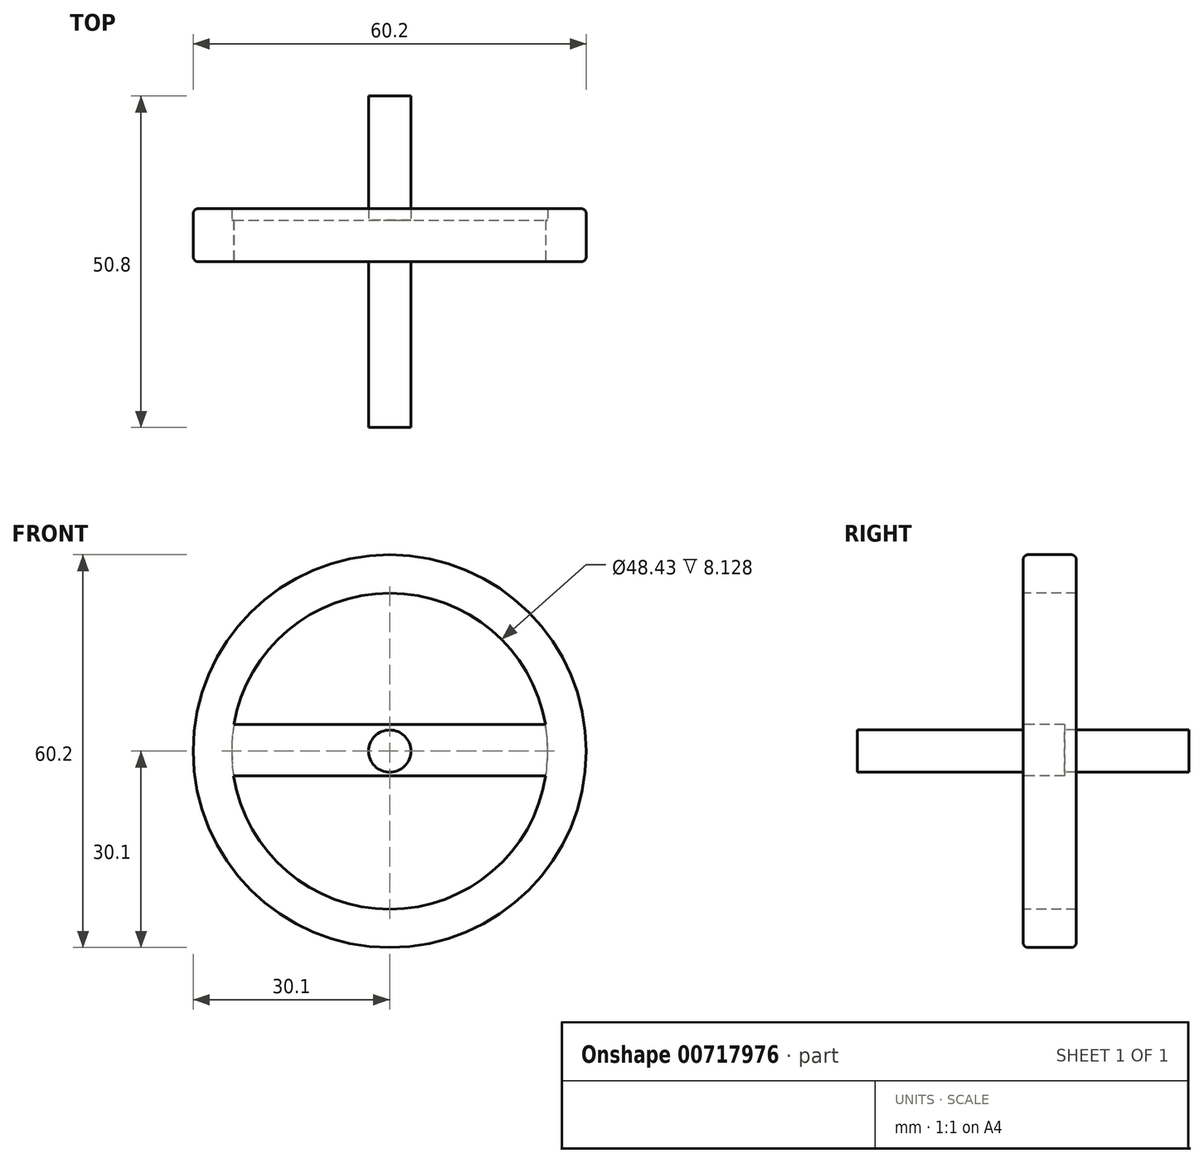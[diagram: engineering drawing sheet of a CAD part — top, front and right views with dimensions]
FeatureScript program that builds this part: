
annotation { "Feature Type Name" : "Feature", "Feature Type Description" : "" }
export const myFeature = defineFeature(function(context is Context, id is Id, definition is map)
    precondition{}
    {
        {
            var Q0;
            Q0=qCreatedBy(makeId("Front.planeOp"),FACE);
            var sketch = newSketch(context, id + "F0", { "sketchPlane" : qUnion([Q0])});
            skCircle(sketch, "E0", {"center": v(0, 0) * mm, "radius": 30.1 * mm});
            skSolve(sketch);
        }
        {
            var Q0;
            Q0 = qSketchRegion(id + "F0", true);
            extrude(context, id + "F1", {"entities" : qUnion([Q0]), "depth" : 8.13 * mm, "offsetDistance" : 25.4 * mm});
        }
        {
            var Q0;
            Q0=makeQuery(id+"F1.opExtrude","CAP_FACE",FACE,{"disambiguationData":[OSD([sQuery(id+"F0.wireOp",EDGE,"E0")])],"isStart":false});
            var sketch = newSketch(context, id + "F2", { "sketchPlane" : qUnion([Q0])});
            skCircle(sketch, "E1", {"center": v(0, 0) * mm, "radius": 24.22 * mm});
            skSolve(sketch);
        }
        {
            var Q0;
            Q0 = qSketchRegion(id + "F2", true);
            extrude(context, id + "F3", {"entities" : qUnion([Q0]), "operationType" : NewBodyOperationType.REMOVE, "oppositeDirection" : true, "depth" : 25.4 * mm, "offsetDistance" : 25.4 * mm});
        }
        {
            var Q0;
            Q0=makeQuery(id+"F1.opExtrude","CAP_FACE",FACE,{"disambiguationData":[OSD([sQuery(id+"F0.wireOp",EDGE,"E0")])],"isStart":false});
            var sketch = newSketch(context, id + "F4", { "sketchPlane" : qUnion([Q0])});
            skLineSegment(sketch, "E2.bottom", {"start": v(-28.38, 4.08) * mm, "end": v(26.3, 4.08) * mm});
            skLineSegment(sketch, "E2.top", {"start": v(-28.38, -3.8) * mm, "end": v(26.3, -3.8) * mm});
            skLineSegment(sketch, "E2.left", {"start": v(-28.38, 4.08) * mm, "end": v(-28.38, -3.8) * mm});
            skLineSegment(sketch, "E2.right", {"start": v(26.3, 4.08) * mm, "end": v(26.3, -3.8) * mm});
            skSolve(sketch);
        }
        {
            var Q0;
            Q0 = qSketchRegion(id + "F4", true);
            extrude(context, id + "F5", {"entities" : qUnion([Q0]), "operationType" : NewBodyOperationType.ADD, "oppositeDirection" : true, "depth" : 6.35 * mm, "offsetDistance" : 25.4 * mm});
        }
        {
            var Q0;
            Q0=makeQuery(id+"F5.boolean.opBoolean","MERGE",FACE,{"derivedFrom":[makeQuery(id+"F1.opExtrude","CAP_FACE",FACE,{"disambiguationData":[OSD([sQuery(id+"F0.wireOp",EDGE,"E0")])],"isStart":false}),makeQuery(id+"F5.opExtrude","CAP_FACE",FACE,{"disambiguationData":[OSD([sQuery(id+"F4.wireOp",EDGE,"E2.bottom"),sQuery(id+"F4.wireOp",EDGE,"E2.top"),sQuery(id+"F4.wireOp",EDGE,"E2.left"),sQuery(id+"F4.wireOp",EDGE,"E2.right")])],"isStart":true})]});
            var sketch = newSketch(context, id + "F6", { "sketchPlane" : qUnion([Q0])});
            skCircle(sketch, "E3", {"center": v(0, 0) * mm, "radius": 3.24 * mm});
            skSolve(sketch);
        }
        {
            var Q0;
            Q0 = qSketchRegion(id + "F6", true);
            extrude(context, id + "F7", {"entities" : qUnion([Q0]), "operationType" : NewBodyOperationType.ADD, "depth" : 25.4 * mm, "offsetDistance" : 25.4 * mm});
        }
        {
            var Q0;
            Q0 = qSketchRegion(id + "F6", true);
            extrude(context, id + "F8", {"entities" : qUnion([Q0]), "operationType" : NewBodyOperationType.ADD, "oppositeDirection" : true, "depth" : 25.4 * mm, "offsetDistance" : 25.4 * mm});
        }
        {
            var Q0;
            Q0=makeQuery(id+"F1.opExtrude","CAP_EDGE",EDGE,{"disambiguationData":[OSD([sQuery(id+"F0.wireOp",EDGE,"E0")])],"isStart":true});
            var Q1;
            Q1=makeQuery(id+"F1.opExtrude","CAP_EDGE",EDGE,{"disambiguationData":[OSD([sQuery(id+"F0.wireOp",EDGE,"E0")])],"isStart":false});
            fillet(context, id + "F9", {"entities" : qUnion([Q0, Q1]), "radius" : 0.76 * mm, "tangentPropagation" : true, "allowEdgeOverflow" : false});
        }
    });
